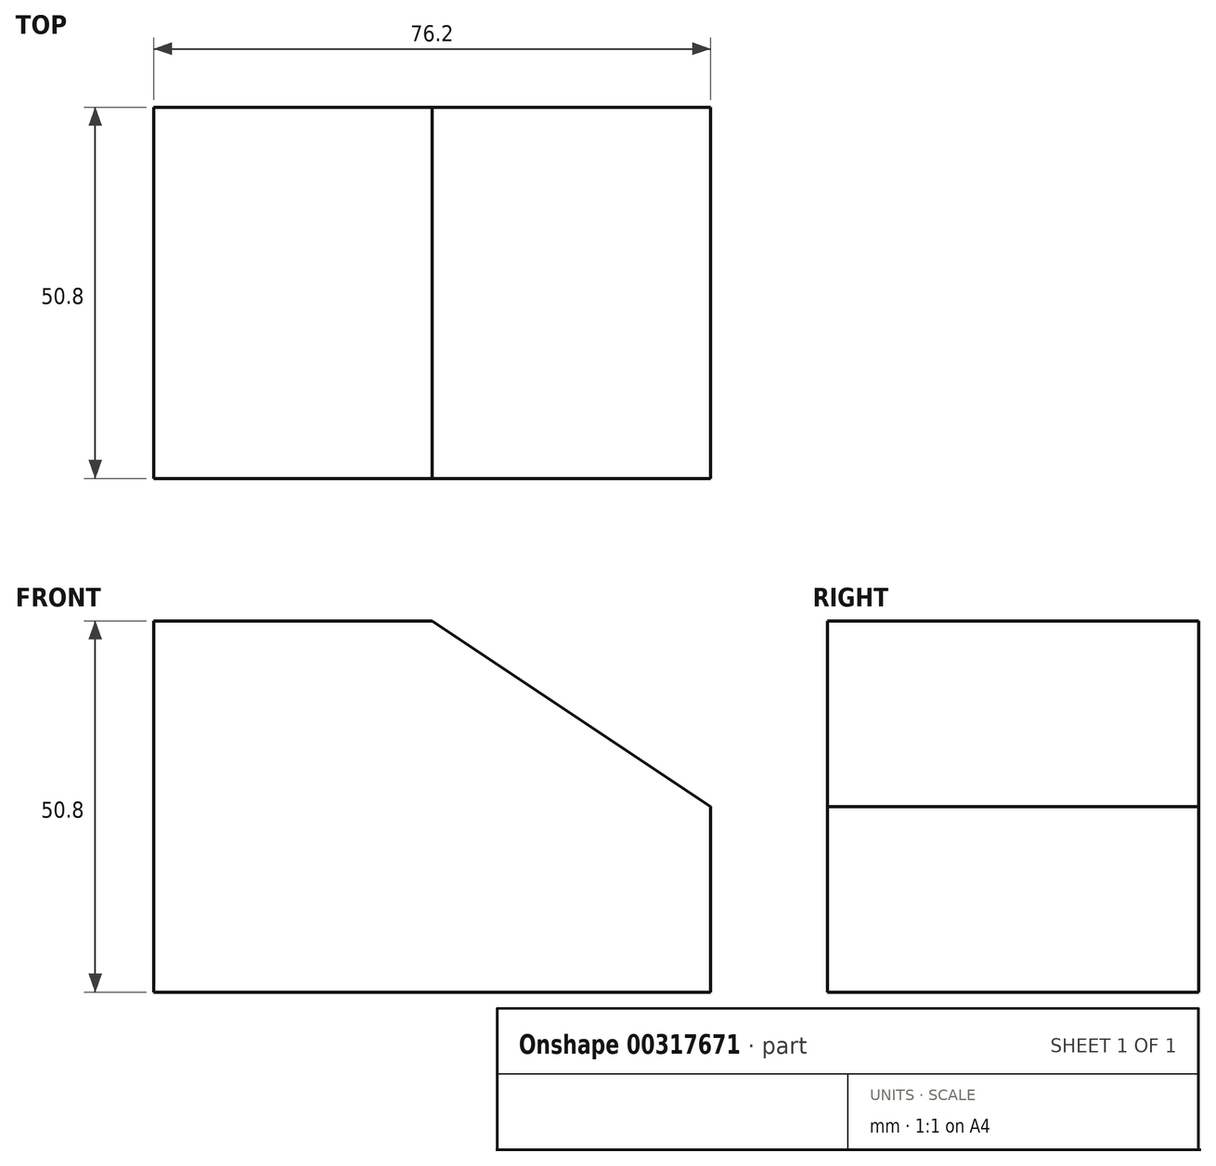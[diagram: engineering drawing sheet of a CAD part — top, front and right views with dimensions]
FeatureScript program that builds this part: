
annotation { "Feature Type Name" : "Feature", "Feature Type Description" : "" }
export const myFeature = defineFeature(function(context is Context, id is Id, definition is map)
    precondition{}
    {
        {
            var Q0;
            Q0=qCreatedBy(makeId("Front.planeOp"),FACE);
            var sketch = newSketch(context, id + "F0", { "sketchPlane" : qUnion([Q0])});
            skLineSegment(sketch, "E0", {"start": v(-25.98, -32.62) * mm, "end": v(50.22, -32.62) * mm});
            skLineSegment(sketch, "E1", {"start": v(-25.98, -32.62) * mm, "end": v(-25.98, 18.18) * mm});
            skLineSegment(sketch, "E2", {"start": v(-25.98, 18.18) * mm, "end": v(12.12, 18.18) * mm});
            skLineSegment(sketch, "E3", {"start": v(50.22, -7.22) * mm, "end": v(50.22, -32.62) * mm});
            skLineSegment(sketch, "E4", {"start": v(12.12, 18.18) * mm, "end": v(50.22, -7.22) * mm});
            skSolve(sketch);
        }
        {
            var Q0;
            Q0 = qSketchRegion(id + "F0", true);
            extrude(context, id + "F1", {"entities" : qUnion([Q0]), "depth" : 50.8 * mm});
        }
    });
